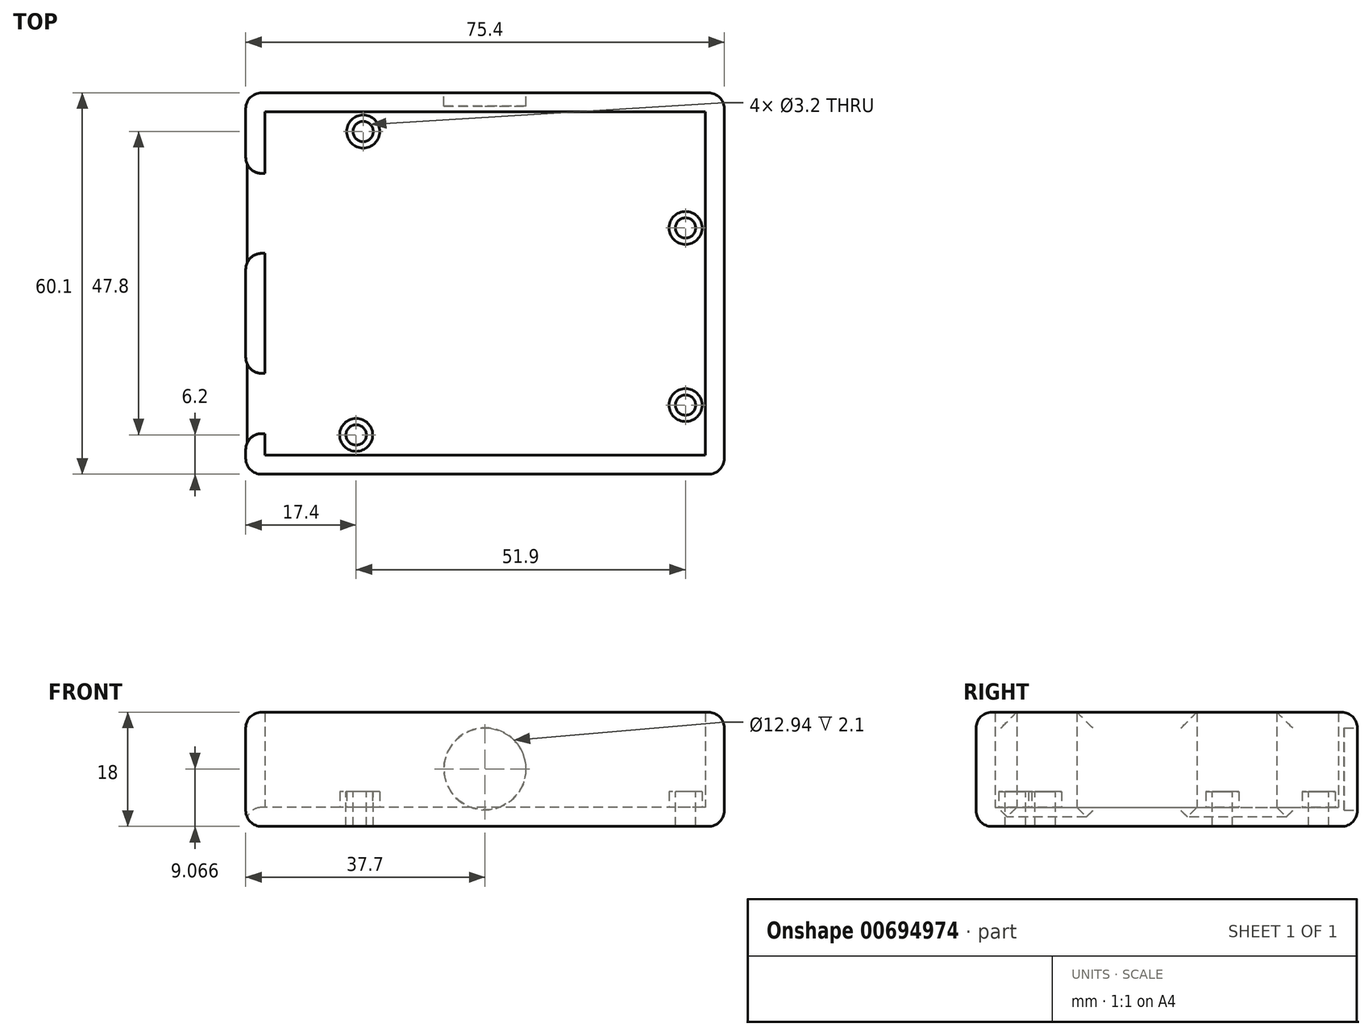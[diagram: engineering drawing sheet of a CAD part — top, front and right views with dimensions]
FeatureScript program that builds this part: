
annotation { "Feature Type Name" : "Feature", "Feature Type Description" : "" }
export const myFeature = defineFeature(function(context is Context, id is Id, definition is map)
    precondition{}
    {
        {
            var Q0;
            Q0=qCreatedBy(makeId("Top.planeOp"),FACE);
            var sketch = newSketch(context, id + "F0", { "sketchPlane" : qUnion([Q0])});
            skLineSegment(sketch, "E0.bottom", {"start": v(34.3, -26.65) * mm, "end": v(-34.3, -26.65) * mm});
            skLineSegment(sketch, "E0.top", {"start": v(34.3, 26.65) * mm, "end": v(-34.3, 26.65) * mm});
            skLineSegment(sketch, "E0.left", {"start": v(34.3, -26.65) * mm, "end": v(34.3, 26.65) * mm});
            skLineSegment(sketch, "E0.right", {"start": v(-34.3, -26.65) * mm, "end": v(-34.3, 26.65) * mm});
            skPoint(sketch, "E0.middle", {"position": v(0, 0) * mm});
            skCircle(sketch, "E1", {"center": v(-19.2, 23.95) * mm, "radius": 1.6 * mm});
            skCircle(sketch, "E2", {"center": v(31.6, 8.75) * mm, "radius": 1.6 * mm});
            skCircle(sketch, "E3", {"center": v(31.6, -19.15) * mm, "radius": 1.6 * mm});
            skCircle(sketch, "E4", {"center": v(-20.3, -23.85) * mm, "radius": 1.6 * mm});
            skLineSegment(sketch, "E5.0", {"start": v(34.7, 27.05) * mm, "end": v(-34.7, 27.05) * mm});
            skLineSegment(sketch, "E5.1", {"start": v(34.7, -27.05) * mm, "end": v(34.7, 27.05) * mm});
            skLineSegment(sketch, "E5.2", {"start": v(34.7, -27.05) * mm, "end": v(-34.7, -27.05) * mm});
            skLineSegment(sketch, "E5.3", {"start": v(-34.7, -27.05) * mm, "end": v(-34.7, 27.05) * mm});
            skLineSegment(sketch, "E6.0", {"start": v(37.7, 30.05) * mm, "end": v(-37.7, 30.05) * mm});
            skLineSegment(sketch, "E6.1", {"start": v(37.7, -30.05) * mm, "end": v(37.7, 30.05) * mm});
            skLineSegment(sketch, "E6.2", {"start": v(37.7, -30.05) * mm, "end": v(-37.7, -30.05) * mm});
            skLineSegment(sketch, "E6.3", {"start": v(-37.7, -30.05) * mm, "end": v(-37.7, 30.05) * mm});
            skLineSegment(sketch, "E7.bottom", {"start": v(-24, 5.05) * mm, "end": v(-40.5, 5.05) * mm});
            skLineSegment(sketch, "E7.top", {"start": v(-24, 17.05) * mm, "end": v(-40.5, 17.05) * mm});
            skLineSegment(sketch, "E7.left", {"start": v(-24, 5.05) * mm, "end": v(-24, 17.05) * mm});
            skLineSegment(sketch, "E7.right", {"start": v(-40.5, 5.05) * mm, "end": v(-40.5, 17.05) * mm});
            skPoint(sketch, "E7.middle", {"position": v(-32.25, 11.05) * mm});
            skLineSegment(sketch, "E8.bottom", {"start": v(-24.8, -23.35) * mm, "end": v(-39.3, -23.35) * mm});
            skLineSegment(sketch, "E8.top", {"start": v(-24.8, -14.45) * mm, "end": v(-39.3, -14.45) * mm});
            skLineSegment(sketch, "E8.left", {"start": v(-24.8, -23.35) * mm, "end": v(-24.8, -14.45) * mm});
            skLineSegment(sketch, "E8.right", {"start": v(-39.3, -23.35) * mm, "end": v(-39.3, -14.45) * mm});
            skPoint(sketch, "E8.middle", {"position": v(-32.05, -18.9) * mm});
            skCircle(sketch, "E9.0", {"center": v(-19.2, 23.95) * mm, "radius": 2.6 * mm});
            skCircle(sketch, "E10.0", {"center": v(-20.3, -23.85) * mm, "radius": 2.6 * mm});
            skCircle(sketch, "E11.0", {"center": v(31.6, -19.15) * mm, "radius": 2.6 * mm});
            skCircle(sketch, "E12.0", {"center": v(31.6, 8.75) * mm, "radius": 2.6 * mm});
            skLineSegment(sketch, "E13.0", {"start": v(-23.7, 4.75) * mm, "end": v(-40.8, 4.75) * mm});
            skLineSegment(sketch, "E13.1", {"start": v(-23.7, 4.75) * mm, "end": v(-23.7, 17.35) * mm});
            skLineSegment(sketch, "E13.2", {"start": v(-23.7, 17.35) * mm, "end": v(-40.8, 17.35) * mm});
            skLineSegment(sketch, "E13.3", {"start": v(-40.8, 4.75) * mm, "end": v(-40.8, 17.35) * mm});
            skLineSegment(sketch, "E14.0", {"start": v(-24.5, -14.15) * mm, "end": v(-39.6, -14.15) * mm});
            skLineSegment(sketch, "E14.1", {"start": v(-24.5, -23.65) * mm, "end": v(-24.5, -14.15) * mm});
            skLineSegment(sketch, "E14.2", {"start": v(-24.5, -23.65) * mm, "end": v(-39.6, -23.65) * mm});
            skLineSegment(sketch, "E14.3", {"start": v(-39.6, -23.65) * mm, "end": v(-39.6, -14.15) * mm});
            skSolve(sketch);
        }
        {
            var Q0;
            {var subQ4=sQuery(id+"F0.wireOp",EDGE,"E5.0");Q0=makeQuery(id+"F0.imprint","IMPRINT",FACE,{"disambiguationData":[TD([[makeQuery(id+"F0.imprint","IMPRINT",EDGE,{"derivedFrom":subQ4}),-1.0]])]});}
            var Q1;
            {var subQ0=sQuery(id+"F0.wireOp",EDGE,"E8.top");var subQ1=sQuery(id+"F0.wireOp",EDGE,"E0.right");var subQ2=makeQuery(id+"F0.imprint","INTERSECT",VERTEX,{"derivedFrom":[subQ1,subQ0]});Q1=makeQuery(id+"F0.imprint","IMPRINT",FACE,{"disambiguationData":[TD([[makeQuery(id+"F0.imprint","IMPRINT",EDGE,{"disambiguationData":[TD([[subQ2,-1.0]])],"derivedFrom":subQ1}),1.0]])]});}
            var Q2;
            {var subQ0=sQuery(id+"F0.wireOp",EDGE,"E8.bottom");var subQ1=sQuery(id+"F0.wireOp",EDGE,"E0.right");var subQ2=makeQuery(id+"F0.imprint","INTERSECT",VERTEX,{"derivedFrom":[subQ1,subQ0]});Q2=makeQuery(id+"F0.imprint","IMPRINT",FACE,{"disambiguationData":[TD([[makeQuery(id+"F0.imprint","IMPRINT",EDGE,{"disambiguationData":[TD([[subQ2,-1.0]])],"derivedFrom":subQ1}),1.0]])]});}
            var Q3;
            {var subQ0=sQuery(id+"F0.wireOp",EDGE,"E8.bottom");var subQ1=sQuery(id+"F0.wireOp",EDGE,"E0.right");var subQ2=makeQuery(id+"F0.imprint","INTERSECT",VERTEX,{"derivedFrom":[subQ1,subQ0]});Q3=makeQuery(id+"F0.imprint","IMPRINT",FACE,{"disambiguationData":[TD([[makeQuery(id+"F0.imprint","IMPRINT",EDGE,{"disambiguationData":[TD([[subQ2,-1.0]])],"derivedFrom":subQ1}),-1.0]])]});}
            var Q4;
            {var subQ4=sQuery(id+"F0.wireOp",EDGE,"E0.bottom");Q4=makeQuery(id+"F0.imprint","IMPRINT",FACE,{"disambiguationData":[TD([[makeQuery(id+"F0.imprint","IMPRINT",EDGE,{"derivedFrom":subQ4}),-1.0]])]});}
            var Q5;
            {var subQ10=sQuery(id+"F0.wireOp",EDGE,"E0.bottom");Q5=makeQuery(id+"F0.imprint","IMPRINT",FACE,{"disambiguationData":[TD([[makeQuery(id+"F0.imprint","IMPRINT",EDGE,{"derivedFrom":subQ10}),1.0]])]});}
            var Q6;
            {var subQ5=sQuery(id+"F0.wireOp",EDGE,"E7.left");Q6=makeQuery(id+"F0.imprint","IMPRINT",FACE,{"disambiguationData":[TD([[makeQuery(id+"F0.imprint","IMPRINT",EDGE,{"derivedFrom":subQ5}),1.0]])]});}
            var Q7;
            {var subQ0=sQuery(id+"F0.wireOp",EDGE,"E7.bottom");var subQ1=sQuery(id+"F0.wireOp",EDGE,"E5.3");var subQ2=makeQuery(id+"F0.imprint","INTERSECT",VERTEX,{"derivedFrom":[subQ1,subQ0]});Q7=makeQuery(id+"F0.imprint","IMPRINT",FACE,{"disambiguationData":[TD([[makeQuery(id+"F0.imprint","IMPRINT",EDGE,{"disambiguationData":[TD([[subQ2,-1.0]])],"derivedFrom":subQ1}),1.0]])]});}
            var Q8;
            {var subQ0=sQuery(id+"F0.wireOp",EDGE,"E7.bottom");var subQ1=sQuery(id+"F0.wireOp",EDGE,"E0.right");var subQ2=makeQuery(id+"F0.imprint","INTERSECT",VERTEX,{"derivedFrom":[subQ1,subQ0]});Q8=makeQuery(id+"F0.imprint","IMPRINT",FACE,{"disambiguationData":[TD([[makeQuery(id+"F0.imprint","IMPRINT",EDGE,{"disambiguationData":[TD([[subQ2,-1.0]])],"derivedFrom":subQ1}),1.0]])]});}
            var Q9;
            {var subQ0=sQuery(id+"F0.wireOp",EDGE,"E8.bottom");var subQ1=sQuery(id+"F0.wireOp",EDGE,"E5.3");var subQ2=makeQuery(id+"F0.imprint","INTERSECT",VERTEX,{"derivedFrom":[subQ1,subQ0]});Q9=makeQuery(id+"F0.imprint","IMPRINT",FACE,{"disambiguationData":[TD([[makeQuery(id+"F0.imprint","IMPRINT",EDGE,{"disambiguationData":[TD([[subQ2,-1.0]])],"derivedFrom":subQ1}),1.0]])]});}
            var Q10;
            {var subQ0=sQuery(id+"F0.wireOp",EDGE,"E8.top");var subQ1=sQuery(id+"F0.wireOp",EDGE,"E5.3");var subQ2=makeQuery(id+"F0.imprint","INTERSECT",VERTEX,{"derivedFrom":[subQ1,subQ0]});Q10=makeQuery(id+"F0.imprint","IMPRINT",FACE,{"disambiguationData":[TD([[makeQuery(id+"F0.imprint","IMPRINT",EDGE,{"disambiguationData":[TD([[subQ2,-1.0]])],"derivedFrom":subQ1}),1.0]])]});}
            var Q11;
            Q11=makeQuery(id+"F0.imprint","IMPRINT",FACE,{"disambiguationData":[TD([[makeQuery(id+"F0.imprint","IMPRINT",EDGE,{"derivedFrom":sQuery(id+"F0.wireOp",EDGE,"E1")}),-1.0]])]});
            var Q12;
            Q12=makeQuery(id+"F0.imprint","IMPRINT",FACE,{"disambiguationData":[TD([[makeQuery(id+"F0.imprint","IMPRINT",EDGE,{"derivedFrom":sQuery(id+"F0.wireOp",EDGE,"E4")}),-1.0]])]});
            var Q13;
            Q13=makeQuery(id+"F0.imprint","IMPRINT",FACE,{"disambiguationData":[TD([[makeQuery(id+"F0.imprint","IMPRINT",EDGE,{"derivedFrom":sQuery(id+"F0.wireOp",EDGE,"E3")}),-1.0]])]});
            var Q14;
            Q14=makeQuery(id+"F0.imprint","IMPRINT",FACE,{"disambiguationData":[TD([[makeQuery(id+"F0.imprint","IMPRINT",EDGE,{"derivedFrom":sQuery(id+"F0.wireOp",EDGE,"E2")}),-1.0]])]});
            var Q15;
            {var subQ0=sQuery(id+"F0.wireOp",EDGE,"E13.0");var subQ1=sQuery(id+"F0.wireOp",EDGE,"E5.3");var subQ2=makeQuery(id+"F0.imprint","INTERSECT",VERTEX,{"derivedFrom":[subQ1,subQ0]});Q15=makeQuery(id+"F0.imprint","IMPRINT",FACE,{"disambiguationData":[TD([[makeQuery(id+"F0.imprint","IMPRINT",EDGE,{"disambiguationData":[TD([[subQ2,-1.0]])],"derivedFrom":subQ1}),1.0]])]});}
            var Q16;
            {var subQ0=sQuery(id+"F0.wireOp",EDGE,"E13.0");var subQ1=sQuery(id+"F0.wireOp",EDGE,"E0.right");var subQ2=makeQuery(id+"F0.imprint","INTERSECT",VERTEX,{"derivedFrom":[subQ1,subQ0]});Q16=makeQuery(id+"F0.imprint","IMPRINT",FACE,{"disambiguationData":[TD([[makeQuery(id+"F0.imprint","IMPRINT",EDGE,{"disambiguationData":[TD([[subQ2,-1.0]])],"derivedFrom":subQ1}),1.0]])]});}
            var Q17;
            {var subQ0=sQuery(id+"F0.wireOp",EDGE,"E7.left");Q17=makeQuery(id+"F0.imprint","IMPRINT",FACE,{"disambiguationData":[TD([[makeQuery(id+"F0.imprint","IMPRINT",EDGE,{"derivedFrom":subQ0}),-1.0]])]});}
            var Q18;
            {var subQ0=sQuery(id+"F0.wireOp",EDGE,"E14.0");var subQ1=sQuery(id+"F0.wireOp",EDGE,"E0.right");var subQ2=makeQuery(id+"F0.imprint","INTERSECT",VERTEX,{"derivedFrom":[subQ1,subQ0]});Q18=makeQuery(id+"F0.imprint","IMPRINT",FACE,{"disambiguationData":[TD([[makeQuery(id+"F0.imprint","IMPRINT",EDGE,{"disambiguationData":[TD([[subQ2,-1.0]])],"derivedFrom":subQ1}),1.0]])]});}
            var Q19;
            {var subQ0=sQuery(id+"F0.wireOp",EDGE,"E14.0");var subQ1=sQuery(id+"F0.wireOp",EDGE,"E5.3");var subQ2=makeQuery(id+"F0.imprint","INTERSECT",VERTEX,{"derivedFrom":[subQ1,subQ0]});Q19=makeQuery(id+"F0.imprint","IMPRINT",FACE,{"disambiguationData":[TD([[makeQuery(id+"F0.imprint","IMPRINT",EDGE,{"disambiguationData":[TD([[subQ2,-1.0]])],"derivedFrom":subQ1}),1.0]])]});}
            var Q20;
            {var subQ0=sQuery(id+"F0.wireOp",EDGE,"E8.left");Q20=makeQuery(id+"F0.imprint","IMPRINT",FACE,{"disambiguationData":[TD([[makeQuery(id+"F0.imprint","IMPRINT",EDGE,{"derivedFrom":subQ0}),-1.0]])]});}
            var Q21;
            {var subQ0=sQuery(id+"F0.wireOp",EDGE,"E7.top");var subQ1=sQuery(id+"F0.wireOp",EDGE,"E5.3");var subQ2=makeQuery(id+"F0.imprint","INTERSECT",VERTEX,{"derivedFrom":[subQ1,subQ0]});Q21=makeQuery(id+"F0.imprint","IMPRINT",FACE,{"disambiguationData":[TD([[makeQuery(id+"F0.imprint","IMPRINT",EDGE,{"disambiguationData":[TD([[subQ2,-1.0]])],"derivedFrom":subQ1}),1.0]])]});}
            var Q22;
            {var subQ0=sQuery(id+"F0.wireOp",EDGE,"E7.top");var subQ1=sQuery(id+"F0.wireOp",EDGE,"E0.right");var subQ2=makeQuery(id+"F0.imprint","INTERSECT",VERTEX,{"derivedFrom":[subQ1,subQ0]});Q22=makeQuery(id+"F0.imprint","IMPRINT",FACE,{"disambiguationData":[TD([[makeQuery(id+"F0.imprint","IMPRINT",EDGE,{"disambiguationData":[TD([[subQ2,-1.0]])],"derivedFrom":subQ1}),1.0]])]});}
            var Q23;
            {var subQ0=sQuery(id+"F0.wireOp",EDGE,"E14.2");var subQ1=sQuery(id+"F0.wireOp",EDGE,"E0.right");var subQ2=makeQuery(id+"F0.imprint","INTERSECT",VERTEX,{"derivedFrom":[subQ1,subQ0]});Q23=makeQuery(id+"F0.imprint","IMPRINT",FACE,{"disambiguationData":[TD([[makeQuery(id+"F0.imprint","IMPRINT",EDGE,{"disambiguationData":[TD([[subQ2,-1.0]])],"derivedFrom":subQ1}),1.0]])]});}
            var Q24;
            {var subQ0=sQuery(id+"F0.wireOp",EDGE,"E14.2");var subQ1=sQuery(id+"F0.wireOp",EDGE,"E5.3");var subQ2=makeQuery(id+"F0.imprint","INTERSECT",VERTEX,{"derivedFrom":[subQ1,subQ0]});Q24=makeQuery(id+"F0.imprint","IMPRINT",FACE,{"disambiguationData":[TD([[makeQuery(id+"F0.imprint","IMPRINT",EDGE,{"disambiguationData":[TD([[subQ2,-1.0]])],"derivedFrom":subQ1}),1.0]])]});}
            extrude(context, id + "F1", {"entities" : qUnion([Q0, Q1, Q2, Q3, Q4, Q5, Q6, Q7, Q8, Q9, Q10, Q11, Q12, Q13, Q14, Q15, Q16, Q17, Q18, Q19, Q20, Q21, Q22, Q23, Q24]), "oppositeDirection" : true, "depth" : 3 * mm});
        }
        {
            var Q0;
            {var subQ11=sQuery(id+"F0.wireOp",EDGE,"E5.0");Q0=makeQuery(id+"F0.imprint","IMPRINT",FACE,{"disambiguationData":[TD([[makeQuery(id+"F0.imprint","IMPRINT",EDGE,{"derivedFrom":subQ11}),-1.0]])]});}
            var Q1;
            {var subQ0=sQuery(id+"F0.wireOp",EDGE,"E14.0");var subQ1=sQuery(id+"F0.wireOp",EDGE,"E5.3");var subQ2=makeQuery(id+"F0.imprint","INTERSECT",VERTEX,{"derivedFrom":[subQ1,subQ0]});Q1=makeQuery(id+"F0.imprint","IMPRINT",FACE,{"disambiguationData":[TD([[makeQuery(id+"F0.imprint","IMPRINT",EDGE,{"disambiguationData":[TD([[subQ2,-1.0]])],"derivedFrom":subQ1}),1.0]])]});}
            extrude(context, id + "F2", {"entities" : qUnion([Q0, Q1]), "operationType" : NewBodyOperationType.ADD, "depth" : 15 * mm});
        }
        {
            var Q0;
            Q0=makeQuery(id+"F0.imprint","IMPRINT",FACE,{"disambiguationData":[TD([[makeQuery(id+"F0.imprint","IMPRINT",EDGE,{"derivedFrom":sQuery(id+"F0.wireOp",EDGE,"E4")}),-1.0]])]});
            var Q1;
            Q1=makeQuery(id+"F0.imprint","IMPRINT",FACE,{"disambiguationData":[TD([[makeQuery(id+"F0.imprint","IMPRINT",EDGE,{"derivedFrom":sQuery(id+"F0.wireOp",EDGE,"E1")}),-1.0]])]});
            var Q2;
            Q2=makeQuery(id+"F0.imprint","IMPRINT",FACE,{"disambiguationData":[TD([[makeQuery(id+"F0.imprint","IMPRINT",EDGE,{"derivedFrom":sQuery(id+"F0.wireOp",EDGE,"E2")}),-1.0]])]});
            var Q3;
            Q3=makeQuery(id+"F0.imprint","IMPRINT",FACE,{"disambiguationData":[TD([[makeQuery(id+"F0.imprint","IMPRINT",EDGE,{"derivedFrom":sQuery(id+"F0.wireOp",EDGE,"E3")}),-1.0]])]});
            extrude(context, id + "F3", {"entities" : qUnion([Q0, Q1, Q2, Q3]), "operationType" : NewBodyOperationType.ADD, "depth" : 2.5 * mm});
        }
        {
            var Q0;
            {var subQ0=sQuery(id+"F0.wireOp",EDGE,"E6.2");var subQ1=sQuery(id+"F0.wireOp",EDGE,"E6.1");Q0=makeQuery(id+"F2.boolean.opBoolean","MERGE",EDGE,{"derivedFrom":[makeQuery(id+"F1.opExtrude","SWEPT_EDGE",EDGE,{"disambiguationData":[OSD([subQ1,subQ0])]}),makeQuery(id+"F2.opExtrude","SWEPT_EDGE",EDGE,{"disambiguationData":[OSD([subQ1,subQ0])]})]});}
            var Q1;
            {var subQ0=sQuery(id+"F0.wireOp",EDGE,"E6.1");var subQ1=sQuery(id+"F0.wireOp",EDGE,"E6.0");Q1=makeQuery(id+"F2.boolean.opBoolean","MERGE",EDGE,{"derivedFrom":[makeQuery(id+"F1.opExtrude","SWEPT_EDGE",EDGE,{"disambiguationData":[OSD([subQ1,subQ0])]}),makeQuery(id+"F2.opExtrude","SWEPT_EDGE",EDGE,{"disambiguationData":[OSD([subQ1,subQ0])]})]});}
            var Q2;
            {var subQ0=sQuery(id+"F0.wireOp",EDGE,"E6.3");var subQ1=sQuery(id+"F0.wireOp",EDGE,"E6.0");Q2=makeQuery(id+"F2.boolean.opBoolean","MERGE",EDGE,{"derivedFrom":[makeQuery(id+"F1.opExtrude","SWEPT_EDGE",EDGE,{"disambiguationData":[OSD([subQ1,subQ0])]}),makeQuery(id+"F2.opExtrude","SWEPT_EDGE",EDGE,{"disambiguationData":[OSD([subQ1,subQ0])]})]});}
            var Q3;
            {var subQ0=sQuery(id+"F0.wireOp",EDGE,"E6.3");var subQ1=sQuery(id+"F0.wireOp",EDGE,"E6.2");Q3=makeQuery(id+"F2.boolean.opBoolean","MERGE",EDGE,{"derivedFrom":[makeQuery(id+"F1.opExtrude","SWEPT_EDGE",EDGE,{"disambiguationData":[OSD([subQ1,subQ0])]}),makeQuery(id+"F2.opExtrude","SWEPT_EDGE",EDGE,{"disambiguationData":[OSD([subQ1,subQ0])]})]});}
            var Q4;
            Q4=makeQuery(id+"F2.opExtrude","SWEPT_EDGE",EDGE,{"disambiguationData":[OSD([sQuery(id+"F0.wireOp",EDGE,"E6.3"),sQuery(id+"F0.wireOp",EDGE,"E14.0")])]});
            var Q5;
            Q5=makeQuery(id+"F2.opExtrude","SWEPT_EDGE",EDGE,{"disambiguationData":[OSD([sQuery(id+"F0.wireOp",EDGE,"E6.3"),sQuery(id+"F0.wireOp",EDGE,"E13.2")])]});
            var Q6;
            Q6=makeQuery(id+"F2.opExtrude","SWEPT_EDGE",EDGE,{"disambiguationData":[OSD([sQuery(id+"F0.wireOp",EDGE,"E6.3"),sQuery(id+"F0.wireOp",EDGE,"E13.0")])]});
            var Q7;
            Q7=makeQuery(id+"F2.opExtrude","SWEPT_EDGE",EDGE,{"disambiguationData":[OSD([sQuery(id+"F0.wireOp",EDGE,"E6.3"),sQuery(id+"F0.wireOp",EDGE,"E14.2")])]});
            var Q8;
            {var subQ0=sQuery(id+"F0.wireOp",EDGE,"E5.3");Q8=makeQuery(id+"F2.opExtrude","CAP_EDGE",EDGE,{"disambiguationData":[OSD([subQ0]),TDD([makeQuery(id+"F0.imprint","IMPRINT",EDGE,{"disambiguationData":[TD([[makeQuery(id+"F0.imprint","INTERSECT",VERTEX,{"derivedFrom":[sQuery(id+"F0.wireOp",EDGE,"E5.0"),subQ0]}),1.0]])],"derivedFrom":subQ0})])],"isStart":true});}
            var Q9;
            Q9=makeQuery(id+"F2.opExtrude","CAP_EDGE",EDGE,{"disambiguationData":[OSD([sQuery(id+"F0.wireOp",EDGE,"E5.0")])],"isStart":true});
            var Q10;
            {var subQ0=sQuery(id+"F0.wireOp",EDGE,"E5.3");Q10=makeQuery(id+"F2.opExtrude","CAP_EDGE",EDGE,{"disambiguationData":[OSD([subQ0]),TDD([makeQuery(id+"F0.imprint","IMPRINT",EDGE,{"disambiguationData":[TD([[makeQuery(id+"F0.imprint","INTERSECT",VERTEX,{"derivedFrom":[subQ0,sQuery(id+"F0.wireOp",EDGE,"E14.0")]}),-1.0]])],"derivedFrom":subQ0})])],"isStart":true});}
            var Q11;
            {var subQ0=sQuery(id+"F0.wireOp",EDGE,"E5.3");Q11=makeQuery(id+"F2.opExtrude","CAP_EDGE",EDGE,{"disambiguationData":[OSD([subQ0]),TDD([makeQuery(id+"F0.imprint","IMPRINT",EDGE,{"disambiguationData":[TD([[makeQuery(id+"F0.imprint","INTERSECT",VERTEX,{"derivedFrom":[sQuery(id+"F0.wireOp",EDGE,"E5.2"),subQ0]}),-1.0]])],"derivedFrom":subQ0})])],"isStart":true});}
            var Q12;
            Q12=makeQuery(id+"F2.opExtrude","CAP_EDGE",EDGE,{"disambiguationData":[OSD([sQuery(id+"F0.wireOp",EDGE,"E5.2")])],"isStart":true});
            var Q13;
            Q13=makeQuery(id+"F2.opExtrude","CAP_EDGE",EDGE,{"disambiguationData":[OSD([sQuery(id+"F0.wireOp",EDGE,"E5.1")])],"isStart":true});
            var Q14;
            Q14=makeQuery(id+"F3.opExtrude","CAP_EDGE",EDGE,{"disambiguationData":[OSD([sQuery(id+"F0.wireOp",EDGE,"E12.0")])],"isStart":true});
            var Q15;
            Q15=makeQuery(id+"F3.opExtrude","CAP_EDGE",EDGE,{"disambiguationData":[OSD([sQuery(id+"F0.wireOp",EDGE,"E11.0")])],"isStart":true});
            var Q16;
            Q16=makeQuery(id+"F3.opExtrude","CAP_EDGE",EDGE,{"disambiguationData":[OSD([sQuery(id+"F0.wireOp",EDGE,"E10.0")])],"isStart":true});
            var Q17;
            Q17=makeQuery(id+"F3.opExtrude","CAP_EDGE",EDGE,{"disambiguationData":[OSD([sQuery(id+"F0.wireOp",EDGE,"E9.0")])],"isStart":true});
            var Q18;
            {var subQ0=sQuery(id+"F0.wireOp",EDGE,"E6.3");var subQ1=sQuery(id+"F0.wireOp",EDGE,"E13.0");Q18=makeQuery(id+"F2.boolean.opBoolean","SPLIT",EDGE,{"disambiguationData":[TD([makeQuery(id+"F2.opExtrude","SWEPT_FACE",FACE,{"disambiguationData":[OSD([subQ1])]})])],"derivedFrom":makeQuery(id+"F1.opExtrude","CAP_EDGE",EDGE,{"disambiguationData":[OSD([subQ0])],"isStart":true})});}
            var Q19;
            {var subQ0=sQuery(id+"F0.wireOp",EDGE,"E14.0");var subQ1=sQuery(id+"F0.wireOp",EDGE,"E6.3");Q19=makeQuery(id+"F2.boolean.opBoolean","SPLIT",EDGE,{"disambiguationData":[TD([makeQuery(id+"F2.opExtrude","SWEPT_FACE",FACE,{"disambiguationData":[OSD([subQ0])]})])],"derivedFrom":makeQuery(id+"F1.opExtrude","CAP_EDGE",EDGE,{"disambiguationData":[OSD([subQ1])],"isStart":true})});}
            var Q20;
            Q20=makeQuery(id+"F1.opExtrude","CAP_EDGE",EDGE,{"disambiguationData":[OSD([sQuery(id+"F0.wireOp",EDGE,"E6.1")])],"isStart":false});
            var Q21;
            Q21=makeQuery(id+"F1.opExtrude","CAP_EDGE",EDGE,{"disambiguationData":[OSD([sQuery(id+"F0.wireOp",EDGE,"E6.0")])],"isStart":false});
            var Q22;
            Q22=makeQuery(id+"F1.opExtrude","CAP_EDGE",EDGE,{"disambiguationData":[OSD([sQuery(id+"F0.wireOp",EDGE,"E6.3")])],"isStart":false});
            var Q23;
            Q23=makeQuery(id+"F1.opExtrude","CAP_EDGE",EDGE,{"disambiguationData":[OSD([sQuery(id+"F0.wireOp",EDGE,"E6.2")])],"isStart":false});
            var Q24;
            Q24=makeQuery(id+"F2.opExtrude","CAP_EDGE",EDGE,{"disambiguationData":[OSD([sQuery(id+"F0.wireOp",EDGE,"E6.0")])],"isStart":false});
            var Q25;
            Q25=makeQuery(id+"F2.opExtrude","CAP_EDGE",EDGE,{"disambiguationData":[OSD([sQuery(id+"F0.wireOp",EDGE,"E6.2")])],"isStart":false});
            var Q26;
            Q26=makeQuery(id+"F2.opExtrude","CAP_EDGE",EDGE,{"disambiguationData":[OSD([sQuery(id+"F0.wireOp",EDGE,"E6.1")])],"isStart":false});
            var Q27;
            {var subQ0=sQuery(id+"F0.wireOp",EDGE,"E6.3");Q27=makeQuery(id+"F2.opExtrude","CAP_EDGE",EDGE,{"disambiguationData":[OSD([subQ0]),TDD([makeQuery(id+"F0.imprint","IMPRINT",EDGE,{"disambiguationData":[TD([[makeQuery(id+"F0.imprint","INTERSECT",VERTEX,{"derivedFrom":[subQ0,sQuery(id+"F0.wireOp",EDGE,"E14.0")]}),-1.0]])],"derivedFrom":subQ0})])],"isStart":false});}
            var Q28;
            {var subQ0=sQuery(id+"F0.wireOp",EDGE,"E6.3");Q28=makeQuery(id+"F2.opExtrude","CAP_EDGE",EDGE,{"disambiguationData":[OSD([subQ0]),TDD([makeQuery(id+"F0.imprint","IMPRINT",EDGE,{"disambiguationData":[TD([[makeQuery(id+"F0.imprint","INTERSECT",VERTEX,{"derivedFrom":[sQuery(id+"F0.wireOp",EDGE,"E6.0"),subQ0]}),1.0]])],"derivedFrom":subQ0})])],"isStart":false});}
            var Q29;
            {var subQ0=sQuery(id+"F0.wireOp",EDGE,"E6.3");Q29=makeQuery(id+"F2.opExtrude","CAP_EDGE",EDGE,{"disambiguationData":[OSD([subQ0]),TDD([makeQuery(id+"F0.imprint","IMPRINT",EDGE,{"disambiguationData":[TD([[makeQuery(id+"F0.imprint","INTERSECT",VERTEX,{"derivedFrom":[sQuery(id+"F0.wireOp",EDGE,"E6.2"),subQ0]}),-1.0]])],"derivedFrom":subQ0})])],"isStart":false});}
            fillet(context, id + "F4", {"entities" : qUnion([Q0, Q1, Q2, Q3, Q4, Q5, Q6, Q7, Q8, Q9, Q10, Q11, Q12, Q13, Q14, Q15, Q16, Q17, Q18, Q19, Q20, Q21, Q22, Q23, Q24, Q25, Q26, Q27, Q28, Q29]), "radius" : 2.5 * mm, "tangentPropagation" : true, "allowEdgeOverflow" : false});
        }
        {
            var Q0;
            {var subQ0=sQuery(id+"F0.wireOp",EDGE,"E6.0");Q0=makeQuery(id+"F2.boolean.opBoolean","MERGE",FACE,{"derivedFrom":[makeQuery(id+"F1.opExtrude","SWEPT_FACE",FACE,{"disambiguationData":[OSD([subQ0])]}),makeQuery(id+"F2.opExtrude","SWEPT_FACE",FACE,{"disambiguationData":[OSD([subQ0])]})]});}
            var sketch = newSketch(context, id + "F5", { "sketchPlane" : qUnion([Q0])});
            skCircle(sketch, "E15", {"center": v(0, 6.07) * mm, "radius": 6.47 * mm});
            skSolve(sketch);
        }
        {
            var Q0;
            Q0 = qSketchRegion(id + "F5", true);
            extrude(context, id + "F6", {"entities" : qUnion([Q0]), "operationType" : NewBodyOperationType.REMOVE, "oppositeDirection" : true, "depth" : 2.1 * mm, "offsetDistance" : 25 * mm});
        }
    });
